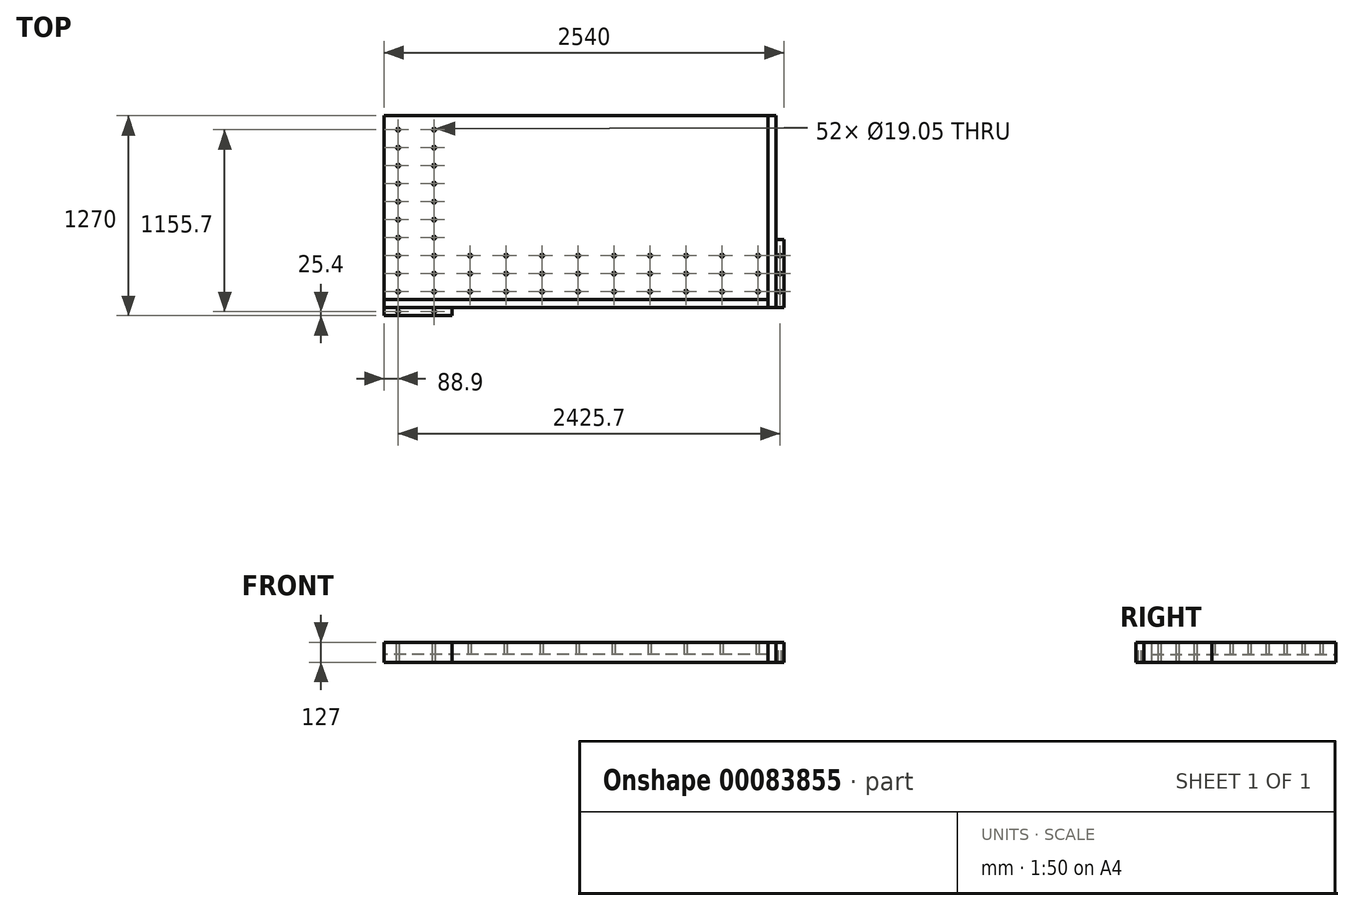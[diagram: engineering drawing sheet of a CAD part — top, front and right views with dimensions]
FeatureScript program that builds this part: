
annotation { "Feature Type Name" : "Feature", "Feature Type Description" : "" }
export const myFeature = defineFeature(function(context is Context, id is Id, definition is map)
    precondition{}
    {
        {
            var Q0;
            Q0=qCreatedBy(makeId("Front.planeOp"),FACE);
            var sketch = newSketch(context, id + "F0", { "sketchPlane" : qUnion([Q0])});
            skLineSegment(sketch, "E0.bottom", {"start": v(1219.2, -38.1) * mm, "end": v(-1219.2, -38.1) * mm});
            skLineSegment(sketch, "E0.top", {"start": v(1219.2, 38.1) * mm, "end": v(-1219.2, 38.1) * mm});
            skLineSegment(sketch, "E0.left", {"start": v(1219.2, -38.1) * mm, "end": v(1219.2, 38.1) * mm});
            skLineSegment(sketch, "E0.right", {"start": v(-1219.2, -38.1) * mm, "end": v(-1219.2, 38.1) * mm});
            skPoint(sketch, "E0.middle", {"position": v(0, 0) * mm});
            skSolve(sketch);
        }
        {
            var Q0;
            Q0=makeQuery(id+"F0.imprint","IMPRINT",FACE,{"disambiguationData":[TD([[makeQuery(id+"F0.imprint","IMPRINT",EDGE,{"derivedFrom":sQuery(id+"F0.wireOp",EDGE,"E0.bottom")}),-1.0]])]});
            extrude(context, id + "F1", {"entities" : qUnion([Q0]), "endBound" : BoundingType.SYMMETRIC, "depth" : 1168.4 * mm});
        }
        {
            var Q0;
            Q0=makeQuery(id+"F1.opExtrude","SWEPT_FACE",FACE,{"disambiguationData":[OSD([sQuery(id+"F0.wireOp",EDGE,"E0.top")])]});
            var sketch = newSketch(context, id + "F2", { "sketchPlane" : qUnion([Q0])});
            skLineSegment(sketch, "E1.0", {"start": v(1219.2, -584.2) * mm, "end": v(-1219.2, -584.2) * mm});
            skLineSegment(sketch, "E2.bottom", {"start": v(-1219.2, -584.2) * mm, "end": v(1219.2, -584.2) * mm});
            skLineSegment(sketch, "E2.top", {"start": v(-1219.2, -635) * mm, "end": v(1219.2, -635) * mm});
            skLineSegment(sketch, "E2.left", {"start": v(-1219.2, -584.2) * mm, "end": v(-1219.2, -635) * mm});
            skLineSegment(sketch, "E2.right", {"start": v(1219.2, -584.2) * mm, "end": v(1219.2, -635) * mm});
            skSolve(sketch);
        }
        {
            var Q0;
            Q0 = qSketchRegion(id + "F2", true);
            extrude(context, id + "F3", {"entities" : qUnion([Q0]), "oppositeDirection" : true, "depth" : 127 * mm});
        }
        {
            var Q0;
            Q0=makeQuery(id+"F1.opExtrude","SWEPT_FACE",FACE,{"disambiguationData":[OSD([sQuery(id+"F0.wireOp",EDGE,"E0.top")])]});
            var sketch = newSketch(context, id + "F4", { "sketchPlane" : qUnion([Q0])});
            skLineSegment(sketch, "E3.0", {"start": v(1219.2, -584.2) * mm, "end": v(1219.2, -635) * mm});
            skLineSegment(sketch, "E4.0", {"start": v(1219.2, -584.2) * mm, "end": v(1219.2, 584.2) * mm});
            skLineSegment(sketch, "E5.bottom", {"start": v(1219.2, -635) * mm, "end": v(1270, -635) * mm});
            skLineSegment(sketch, "E5.top", {"start": v(1219.2, 584.2) * mm, "end": v(1270, 584.2) * mm});
            skLineSegment(sketch, "E5.left", {"start": v(1219.2, -635) * mm, "end": v(1219.2, 584.2) * mm});
            skLineSegment(sketch, "E5.right", {"start": v(1270, -635) * mm, "end": v(1270, 584.2) * mm});
            skLineSegment(sketch, "E6.bottom", {"start": v(1219.2, 584.2) * mm, "end": v(1219.2, 584.2) * mm});
            skLineSegment(sketch, "E6.top", {"start": v(1219.2, 584.2) * mm, "end": v(1219.2, 584.2) * mm});
            skLineSegment(sketch, "E6.left", {"start": v(1219.2, 584.2) * mm, "end": v(1219.2, 584.2) * mm});
            skLineSegment(sketch, "E6.right", {"start": v(1219.2, 584.2) * mm, "end": v(1219.2, 584.2) * mm});
            skSolve(sketch);
        }
        {
            var Q0;
            Q0 = qSketchRegion(id + "F4", true);
            extrude(context, id + "F5", {"entities" : qUnion([Q0]), "oppositeDirection" : true, "depth" : 127 * mm});
        }
        {
            var Q0;
            Q0=makeQuery(id+"F1.opExtrude","SWEPT_FACE",FACE,{"disambiguationData":[OSD([sQuery(id+"F0.wireOp",EDGE,"E0.top")])]});
            var sketch = newSketch(context, id + "F6", { "sketchPlane" : qUnion([Q0])});
            skPoint(sketch, "E7.0", {"position": v(-1219.2, -635) * mm});
            skLineSegment(sketch, "E8.bottom", {"start": v(-1219.2, -635) * mm, "end": v(-787.4, -635) * mm});
            skLineSegment(sketch, "E8.top", {"start": v(-1219.2, -685.8) * mm, "end": v(-787.4, -685.8) * mm});
            skLineSegment(sketch, "E8.left", {"start": v(-1219.2, -635) * mm, "end": v(-1219.2, -685.8) * mm});
            skLineSegment(sketch, "E8.right", {"start": v(-787.4, -635) * mm, "end": v(-787.4, -685.8) * mm});
            skSolve(sketch);
        }
        {
            var Q0;
            Q0 = qSketchRegion(id + "F6", true);
            extrude(context, id + "F7", {"entities" : qUnion([Q0]), "oppositeDirection" : true, "depth" : 127 * mm});
        }
        {
            var Q0;
            Q0=makeQuery(id+"F1.opExtrude","SWEPT_FACE",FACE,{"disambiguationData":[OSD([sQuery(id+"F0.wireOp",EDGE,"E0.top")])]});
            var sketch = newSketch(context, id + "F8", { "sketchPlane" : qUnion([Q0])});
            skPoint(sketch, "E9.0", {"position": v(1270, -635) * mm});
            skLineSegment(sketch, "E10.bottom", {"start": v(1270, -635) * mm, "end": v(1320.8, -635) * mm});
            skLineSegment(sketch, "E10.top", {"start": v(1270, -203.2) * mm, "end": v(1320.8, -203.2) * mm});
            skLineSegment(sketch, "E10.left", {"start": v(1270, -635) * mm, "end": v(1270, -203.2) * mm});
            skLineSegment(sketch, "E10.right", {"start": v(1320.8, -635) * mm, "end": v(1320.8, -203.2) * mm});
            skSolve(sketch);
        }
        {
            var Q0;
            Q0 = qSketchRegion(id + "F8", true);
            extrude(context, id + "F9", {"entities" : qUnion([Q0]), "oppositeDirection" : true, "depth" : 127 * mm});
        }
        {
            var Q0;
            Q0=makeQuery(id+"F1.opExtrude","SWEPT_FACE",FACE,{"disambiguationData":[OSD([sQuery(id+"F0.wireOp",EDGE,"E0.top")])]});
            var sketch = newSketch(context, id + "F10", { "sketchPlane" : qUnion([Q0])});
            skLineSegment(sketch, "E11.0", {"start": v(-1219.2, -584.2) * mm, "end": v(-1219.2, 584.2) * mm});
            skLineSegment(sketch, "E12.0", {"start": v(1219.2, -584.2) * mm, "end": v(-1219.2, -584.2) * mm});
            skCircle(sketch, "E13", {"center": v(-1130.3, -533.4) * mm, "radius": 9.53 * mm});
            skCircle(sketch, "E14.0.1.0", {"center": v(-1130.3, -419.1) * mm, "radius": 9.53 * mm});
            skCircle(sketch, "E14.0.2.0", {"center": v(-1130.3, -304.8) * mm, "radius": 9.53 * mm});
            skCircle(sketch, "E14.0.3.0", {"center": v(-1130.3, -190.5) * mm, "radius": 9.53 * mm});
            skCircle(sketch, "E14.0.4.0", {"center": v(-1130.3, -76.2) * mm, "radius": 9.53 * mm});
            skCircle(sketch, "E14.0.5.0", {"center": v(-1130.3, 38.1) * mm, "radius": 9.53 * mm});
            skCircle(sketch, "E14.0.6.0", {"center": v(-1130.3, 152.4) * mm, "radius": 9.53 * mm});
            skCircle(sketch, "E14.0.7.0", {"center": v(-1130.3, 266.7) * mm, "radius": 9.53 * mm});
            skCircle(sketch, "E14.0.8.0", {"center": v(-1130.3, 381) * mm, "radius": 9.53 * mm});
            skCircle(sketch, "E14.0.9.0", {"center": v(-1130.3, 495.3) * mm, "radius": 9.53 * mm});
            skCircle(sketch, "E14.1.0.0", {"center": v(-901.7, -533.4) * mm, "radius": 9.53 * mm});
            skCircle(sketch, "E14.1.1.0", {"center": v(-901.7, -419.1) * mm, "radius": 9.53 * mm});
            skCircle(sketch, "E14.1.2.0", {"center": v(-901.7, -304.8) * mm, "radius": 9.53 * mm});
            skCircle(sketch, "E14.1.3.0", {"center": v(-901.7, -190.5) * mm, "radius": 9.53 * mm});
            skCircle(sketch, "E14.1.4.0", {"center": v(-901.7, -76.2) * mm, "radius": 9.53 * mm});
            skCircle(sketch, "E14.1.5.0", {"center": v(-901.7, 38.1) * mm, "radius": 9.53 * mm});
            skCircle(sketch, "E14.1.6.0", {"center": v(-901.7, 152.4) * mm, "radius": 9.53 * mm});
            skCircle(sketch, "E14.1.7.0", {"center": v(-901.7, 266.7) * mm, "radius": 9.53 * mm});
            skCircle(sketch, "E14.1.8.0", {"center": v(-901.7, 381) * mm, "radius": 9.53 * mm});
            skCircle(sketch, "E14.1.9.0", {"center": v(-901.7, 495.3) * mm, "radius": 9.53 * mm});
            skLineSegment(sketch, "E14.direction1", {"start": v(-1130.3, -533.4) * mm, "end": v(-901.7, -533.4) * mm, "construction": true});
            skLineSegment(sketch, "E14.direction2", {"start": v(-1130.3, -533.4) * mm, "end": v(-1130.3, -419.1) * mm, "construction": true});
            skCircle(sketch, "E15.1.0.0", {"center": v(-673.1, -533.4) * mm, "radius": 9.53 * mm});
            skCircle(sketch, "E15.1.1.0", {"center": v(-673.1, -419.1) * mm, "radius": 9.53 * mm});
            skCircle(sketch, "E15.1.2.0", {"center": v(-673.1, -304.8) * mm, "radius": 9.53 * mm});
            skCircle(sketch, "E15.2.0.0", {"center": v(-444.5, -533.4) * mm, "radius": 9.53 * mm});
            skCircle(sketch, "E15.2.1.0", {"center": v(-444.5, -419.1) * mm, "radius": 9.53 * mm});
            skCircle(sketch, "E15.2.2.0", {"center": v(-444.5, -304.8) * mm, "radius": 9.53 * mm});
            skCircle(sketch, "E15.3.0.0", {"center": v(-215.9, -533.4) * mm, "radius": 9.53 * mm});
            skCircle(sketch, "E15.3.1.0", {"center": v(-215.9, -419.1) * mm, "radius": 9.53 * mm});
            skCircle(sketch, "E15.3.2.0", {"center": v(-215.9, -304.8) * mm, "radius": 9.53 * mm});
            skCircle(sketch, "E15.4.0.0", {"center": v(12.7, -533.4) * mm, "radius": 9.53 * mm});
            skCircle(sketch, "E15.4.1.0", {"center": v(12.7, -419.1) * mm, "radius": 9.53 * mm});
            skCircle(sketch, "E15.4.2.0", {"center": v(12.7, -304.8) * mm, "radius": 9.53 * mm});
            skCircle(sketch, "E15.5.0.0", {"center": v(241.3, -533.4) * mm, "radius": 9.53 * mm});
            skCircle(sketch, "E15.5.1.0", {"center": v(241.3, -419.1) * mm, "radius": 9.53 * mm});
            skCircle(sketch, "E15.5.2.0", {"center": v(241.3, -304.8) * mm, "radius": 9.53 * mm});
            skCircle(sketch, "E15.6.0.0", {"center": v(469.9, -533.4) * mm, "radius": 9.53 * mm});
            skCircle(sketch, "E15.6.1.0", {"center": v(469.9, -419.1) * mm, "radius": 9.53 * mm});
            skCircle(sketch, "E15.6.2.0", {"center": v(469.9, -304.8) * mm, "radius": 9.53 * mm});
            skCircle(sketch, "E15.7.0.0", {"center": v(698.5, -533.4) * mm, "radius": 9.53 * mm});
            skCircle(sketch, "E15.7.1.0", {"center": v(698.5, -419.1) * mm, "radius": 9.53 * mm});
            skCircle(sketch, "E15.7.2.0", {"center": v(698.5, -304.8) * mm, "radius": 9.53 * mm});
            skCircle(sketch, "E15.8.0.0", {"center": v(927.1, -533.4) * mm, "radius": 9.53 * mm});
            skCircle(sketch, "E15.8.1.0", {"center": v(927.1, -419.1) * mm, "radius": 9.53 * mm});
            skCircle(sketch, "E15.8.2.0", {"center": v(927.1, -304.8) * mm, "radius": 9.53 * mm});
            skLineSegment(sketch, "E15.direction1", {"start": v(-901.7, -533.4) * mm, "end": v(-673.1, -533.4) * mm, "construction": true});
            skLineSegment(sketch, "E15.direction2", {"start": v(-901.7, -533.4) * mm, "end": v(-901.7, -419.1) * mm, "construction": true});
            skCircle(sketch, "E16.0.9.0", {"center": v(1155.7, -533.4) * mm, "radius": 9.53 * mm});
            skCircle(sketch, "E16.0.9.1", {"center": v(1155.7, -419.1) * mm, "radius": 9.53 * mm});
            skCircle(sketch, "E16.0.9.2", {"center": v(1155.7, -304.8) * mm, "radius": 9.53 * mm});
            skSolve(sketch);
        }
        {
            var Q0;
            Q0 = qSketchRegion(id + "F10", true);
            extrude(context, id + "F11", {"entities" : qUnion([Q0]), "operationType" : NewBodyOperationType.REMOVE, "oppositeDirection" : true, "depth" : 76.2 * mm});
        }
        {
            var Q0;
            Q0=makeQuery(id+"F7.opExtrude","CAP_FACE",FACE,{"disambiguationData":[OSD([sQuery(id+"F6.wireOp",EDGE,"E8.bottom"),sQuery(id+"F6.wireOp",EDGE,"E8.top"),sQuery(id+"F6.wireOp",EDGE,"E8.left"),sQuery(id+"F6.wireOp",EDGE,"E8.right")])],"isStart":true});
            var sketch = newSketch(context, id + "F12", { "sketchPlane" : qUnion([Q0])});
            skCircle(sketch, "E17", {"center": v(-1130.3, -660.4) * mm, "radius": 9.53 * mm});
            skCircle(sketch, "E18.1.0.0", {"center": v(-901.7, -660.4) * mm, "radius": 9.53 * mm});
            skLineSegment(sketch, "E18.direction1", {"start": v(-1130.3, -660.4) * mm, "end": v(-901.7, -660.4) * mm, "construction": true});
            skSolve(sketch);
        }
        {
            var Q0;
            Q0 = qSketchRegion(id + "F12", true);
            extrude(context, id + "F13", {"entities" : qUnion([Q0]), "operationType" : NewBodyOperationType.REMOVE, "oppositeDirection" : true, "depth" : 127 * mm});
        }
        {
            var Q0;
            Q0=makeQuery(id+"F9.opExtrude","CAP_FACE",FACE,{"disambiguationData":[OSD([sQuery(id+"F8.wireOp",EDGE,"E10.bottom"),sQuery(id+"F8.wireOp",EDGE,"E10.top"),sQuery(id+"F8.wireOp",EDGE,"E10.left"),sQuery(id+"F8.wireOp",EDGE,"E10.right")])],"isStart":true});
            var sketch = newSketch(context, id + "F14", { "sketchPlane" : qUnion([Q0])});
            skCircle(sketch, "E19", {"center": v(1295.4, -533.4) * mm, "radius": 9.53 * mm});
            skCircle(sketch, "E20.0.1.0", {"center": v(1295.4, -419.1) * mm, "radius": 9.53 * mm});
            skCircle(sketch, "E20.0.2.0", {"center": v(1295.4, -304.8) * mm, "radius": 9.53 * mm});
            skLineSegment(sketch, "E20.direction1", {"start": v(1295.4, -533.4) * mm, "end": v(1324.79, -533.4) * mm, "construction": true});
            skLineSegment(sketch, "E20.direction2", {"start": v(1295.4, -533.4) * mm, "end": v(1295.4, -419.1) * mm, "construction": true});
            skSolve(sketch);
        }
        {
            var Q0;
            Q0 = qSketchRegion(id + "F14", true);
            extrude(context, id + "F15", {"entities" : qUnion([Q0]), "operationType" : NewBodyOperationType.REMOVE, "oppositeDirection" : true, "depth" : 127 * mm});
        }
    });
